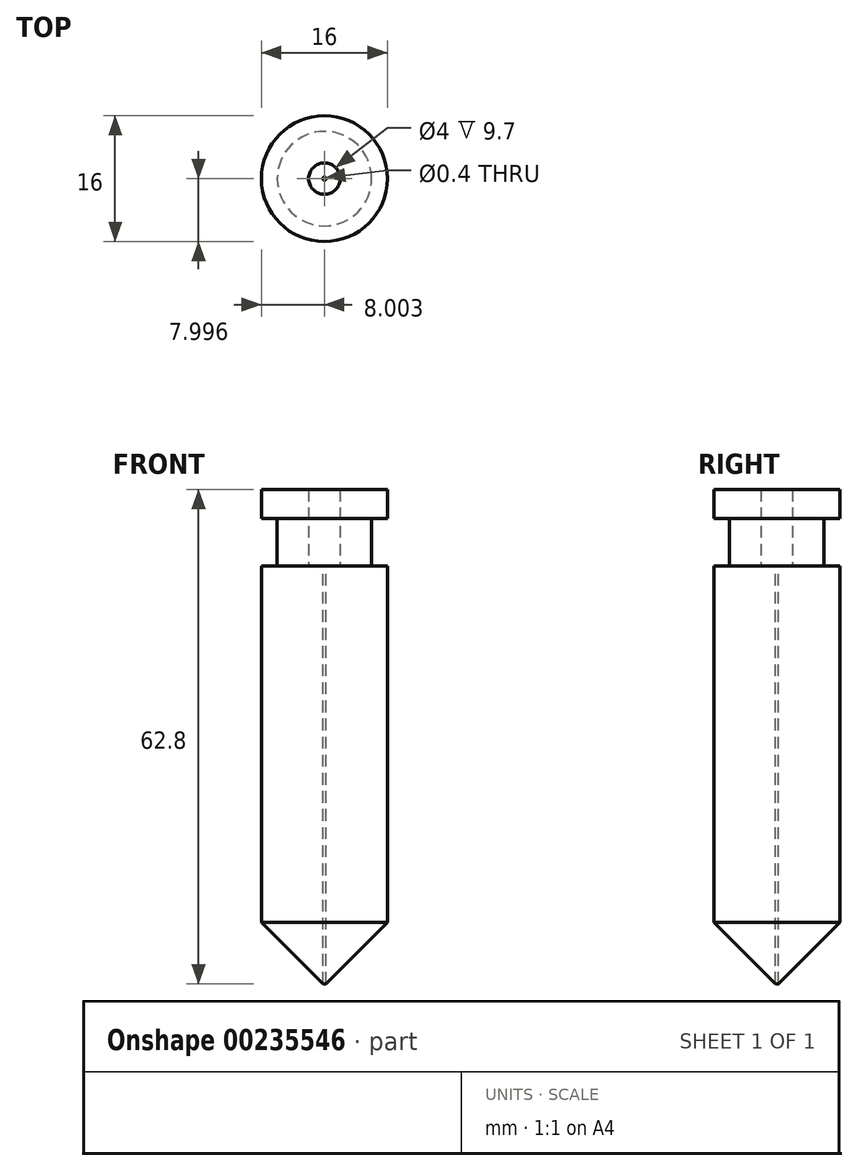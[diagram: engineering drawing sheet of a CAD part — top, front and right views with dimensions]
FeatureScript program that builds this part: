
annotation { "Feature Type Name" : "Feature", "Feature Type Description" : "" }
export const myFeature = defineFeature(function(context is Context, id is Id, definition is map)
    precondition{}
    {
        {
            var Q0;
            Q0=qCreatedBy(makeId("Top.planeOp"),FACE);
            var sketch = newSketch(context, id + "F0", { "sketchPlane" : qUnion([Q0])});
            skCircle(sketch, "E0", {"center": v(-42.4, 33.1) * mm, "radius": 8 * mm});
            skCircle(sketch, "E1", {"center": v(-42.4, 33.1) * mm, "radius": 6 * mm});
            skSolve(sketch);
        }
        {
            var Q0;
            Q0 = qSketchRegion(id + "F0", true);
            var Q1;
            Q1=makeQuery(id+"F0.imprint","IMPRINT",FACE,{"disambiguationData":[TD([[makeQuery(id+"F0.imprint","IMPRINT",EDGE,{"derivedFrom":sQuery(id+"F0.wireOp",EDGE,"E1")}),1.0]])]});
            extrude(context, id + "F1", {"entities" : qUnion([Q0, Q1]), "oppositeDirection" : true, "depth" : 53.3 * mm});
        }
        {
            var Q0;
            Q0=makeQuery(id+"F0.imprint","IMPRINT",FACE,{"disambiguationData":[TD([[makeQuery(id+"F0.imprint","IMPRINT",EDGE,{"derivedFrom":sQuery(id+"F0.wireOp",EDGE,"E1")}),1.0]])]});
            extrude(context, id + "F2", {"entities" : qUnion([Q0]), "operationType" : NewBodyOperationType.ADD, "depth" : 6 * mm});
        }
        {
            var Q0;
            Q0=makeQuery(id+"F0.imprint","IMPRINT",FACE,{"disambiguationData":[TD([[makeQuery(id+"F0.imprint","IMPRINT",EDGE,{"derivedFrom":sQuery(id+"F0.wireOp",EDGE,"E0")}),1.0]])]});
            var Q1;
            Q1=makeQuery(id+"F0.imprint","IMPRINT",FACE,{"disambiguationData":[TD([[makeQuery(id+"F0.imprint","IMPRINT",EDGE,{"derivedFrom":sQuery(id+"F0.wireOp",EDGE,"E1")}),1.0]])]});
            var Q2;
            Q2=sQuery(id+"F0.wireOp",EDGE,"E0");
            var Q3;
            Q3=sQuery(id+"F0.wireOp",EDGE,"E1");
            extrude(context, id + "F3", {"entities" : qUnion([Q0, Q1]), "operationType" : NewBodyOperationType.ADD, "surfaceEntities" : qUnion([Q2, Q3]), "depth" : 9.7 * mm, "hasSecondDirection" : true, "secondDirectionOppositeDirection" : false, "secondDirectionDepth" : 6 * mm});
        }
        {
            var Q0;
            Q0=makeQuery(id+"F1.opExtrude","CAP_EDGE",EDGE,{"disambiguationData":[OSD([sQuery(id+"F0.wireOp",EDGE,"E0")])],"isStart":false});
            chamfer(context, id + "F4", {"entities" : qUnion([Q0]), "width" : 8 * mm, "tangentPropagation" : true});
        }
        {
            var Q0;
            Q0=sQuery(id+"F0.wireOp",VERTEX,"E0.center");
            var Q1;
            Q1=makeQuery(id+"F1.opExtrude","SWEPT_BODY",BODY,{"disambiguationData":[OSD([sQuery(id+"F0.wireOp",EDGE,"E0")])]});
            hole(context, id + "F5", {"style" : HoleStyle.SIMPLE, "endStyle" : HoleEndStyle.BLIND, "oppositeDirection" : true, "holeDiameter" : 4 * mm, "holeDepth" : 20 * mm, "tappedDepth" : 12 * mm, "tapClearance" : 3, "locations" : qUnion([Q0]), "scope" : qUnion([Q1])});
        }
        {
            var Q0;
            Q0=sQuery(id+"F0.wireOp",VERTEX,"E0.center");
            var Q1;
            Q1=makeQuery(id+"F1.opExtrude","SWEPT_BODY",BODY,{"disambiguationData":[OSD([sQuery(id+"F0.wireOp",EDGE,"E0")])]});
            hole(context, id + "F6", {"style" : HoleStyle.SIMPLE, "endStyle" : HoleEndStyle.BLIND, "holeDiameter" : 0.4 * mm, "holeDepth" : 70 * mm, "tappedDepth" : 12 * mm, "tapClearance" : 3, "locations" : qUnion([Q0]), "scope" : qUnion([Q1])});
        }
    });
